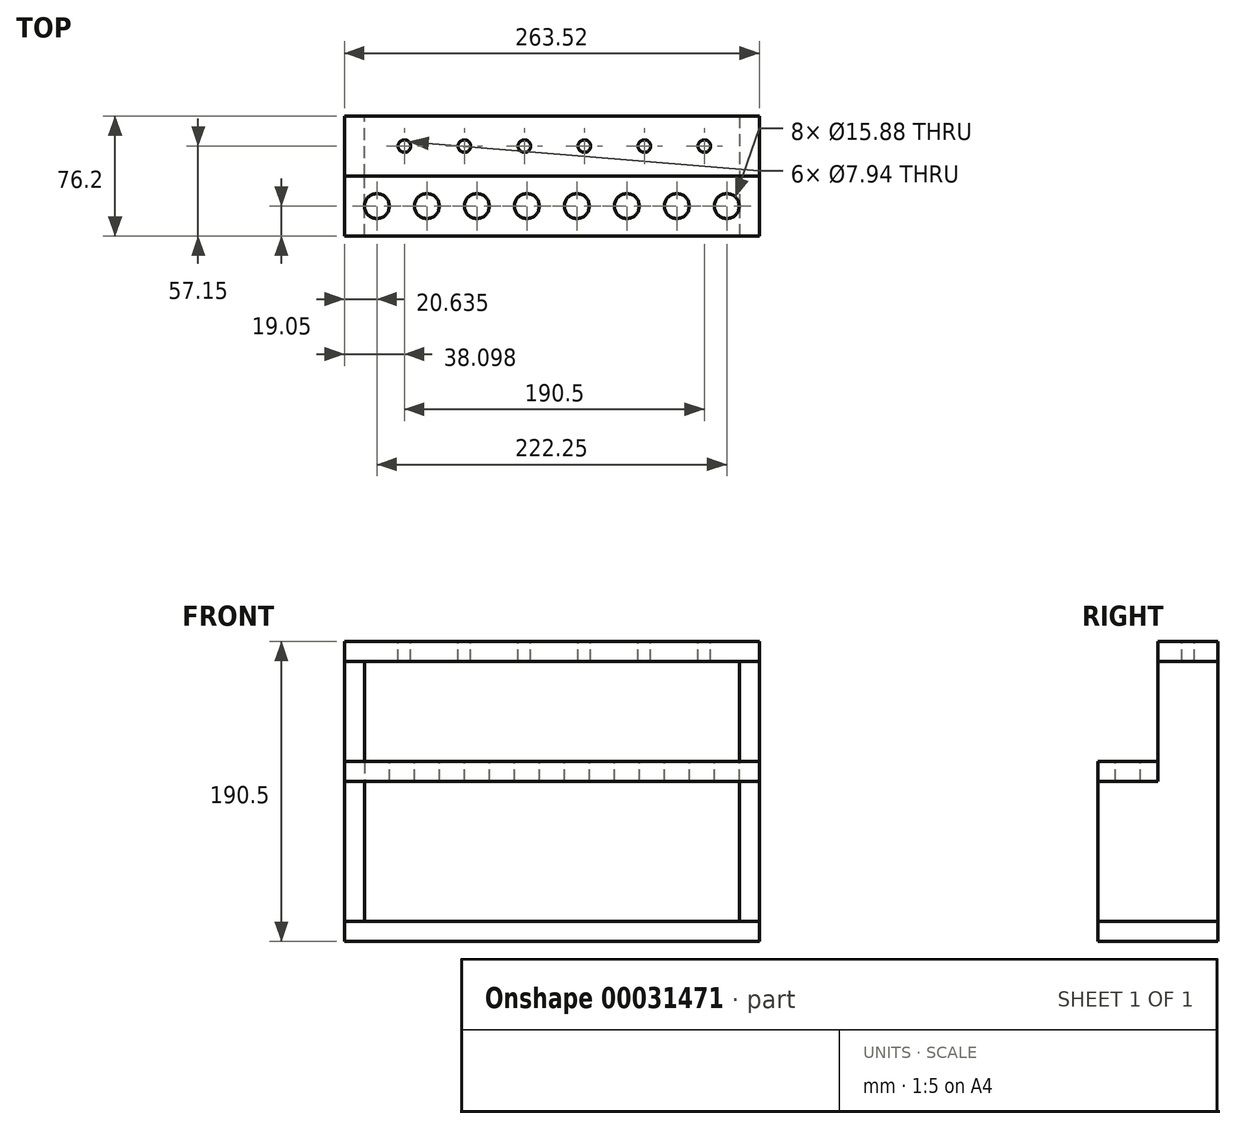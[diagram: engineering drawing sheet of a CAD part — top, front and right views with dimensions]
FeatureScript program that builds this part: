
annotation { "Feature Type Name" : "Feature", "Feature Type Description" : "" }
export const myFeature = defineFeature(function(context is Context, id is Id, definition is map)
    precondition{}
    {
        {
            var Q0;
            Q0=qCreatedBy(makeId("Top.planeOp"),FACE);
            var sketch = newSketch(context, id + "F0", { "sketchPlane" : qUnion([Q0])});
            skLineSegment(sketch, "E0.bottom", {"start": v(-189.07, 76.2) * mm, "end": v(74.45, 76.2) * mm});
            skLineSegment(sketch, "E0.top", {"start": v(-189.07, 0) * mm, "end": v(74.45, 0) * mm});
            skLineSegment(sketch, "E0.left", {"start": v(-189.07, 76.2) * mm, "end": v(-189.07, 0) * mm});
            skLineSegment(sketch, "E0.right", {"start": v(74.45, 76.2) * mm, "end": v(74.45, 0) * mm});
            skSolve(sketch);
        }
        {
            var Q0;
            Q0=makeQuery(id+"F0.imprint","IMPRINT",FACE,{"disambiguationData":[TD([[makeQuery(id+"F0.imprint","IMPRINT",EDGE,{"derivedFrom":sQuery(id+"F0.wireOp",EDGE,"E0.bottom")}),-1.0]])]});
            extrude(context, id + "F1", {"entities" : qUnion([Q0]), "depth" : 12.7 * mm});
        }
        {
            var Q0;
            Q0=makeQuery(id+"F1.opExtrude","CAP_FACE",FACE,{"disambiguationData":[OSD([sQuery(id+"F0.wireOp",EDGE,"E0.bottom"),sQuery(id+"F0.wireOp",EDGE,"E0.top"),sQuery(id+"F0.wireOp",EDGE,"E0.left"),sQuery(id+"F0.wireOp",EDGE,"E0.right")])],"isStart":false});
            var sketch = newSketch(context, id + "F2", { "sketchPlane" : qUnion([Q0])});
            skLineSegment(sketch, "E1.bottom", {"start": v(-189.07, 0) * mm, "end": v(-176.37, 0) * mm});
            skLineSegment(sketch, "E1.top", {"start": v(-189.07, 76.2) * mm, "end": v(-176.37, 76.2) * mm});
            skLineSegment(sketch, "E1.left", {"start": v(-189.07, 0) * mm, "end": v(-189.07, 76.2) * mm});
            skLineSegment(sketch, "E1.right", {"start": v(-176.37, 0) * mm, "end": v(-176.37, 76.2) * mm});
            skSolve(sketch);
        }
        {
            var Q0;
            Q0=makeQuery(id+"F2.imprint","IMPRINT",FACE,{"disambiguationData":[TD([[makeQuery(id+"F2.imprint","IMPRINT",EDGE,{"derivedFrom":sQuery(id+"F2.wireOp",EDGE,"E1.bottom")}),1.0]])]});
            extrude(context, id + "F3", {"entities" : qUnion([Q0]), "depth" : 165.1 * mm});
        }
        {
            var Q0;
            Q0=makeQuery(id+"F3.opExtrude","SWEPT_FACE",FACE,{"disambiguationData":[OSD([sQuery(id+"F2.wireOp",EDGE,"E1.right")])]});
            var sketch = newSketch(context, id + "F4", { "sketchPlane" : qUnion([Q0])});
            skLineSegment(sketch, "E2.bottom", {"start": v(0, 177.8) * mm, "end": v(38.1, 177.8) * mm});
            skLineSegment(sketch, "E2.top", {"start": v(0, 101.6) * mm, "end": v(38.1, 101.6) * mm});
            skLineSegment(sketch, "E2.left", {"start": v(0, 177.8) * mm, "end": v(0, 101.6) * mm});
            skLineSegment(sketch, "E2.right", {"start": v(38.1, 177.8) * mm, "end": v(38.1, 101.6) * mm});
            skSolve(sketch);
        }
        {
            var Q0;
            Q0=makeQuery(id+"F4.imprint","IMPRINT",FACE,{"disambiguationData":[TD([[makeQuery(id+"F4.imprint","IMPRINT",EDGE,{"derivedFrom":sQuery(id+"F4.wireOp",EDGE,"E2.bottom")}),-1.0]])]});
            extrude(context, id + "F5", {"entities" : qUnion([Q0]), "operationType" : NewBodyOperationType.REMOVE, "endBound" : BoundingType.UP_TO_NEXT, "oppositeDirection" : true, "depth" : 25.4 * mm});
        }
        {
            var Q0;
            Q0=makeQuery(id+"F1.opExtrude","CAP_FACE",FACE,{"disambiguationData":[OSD([sQuery(id+"F0.wireOp",EDGE,"E0.bottom"),sQuery(id+"F0.wireOp",EDGE,"E0.top"),sQuery(id+"F0.wireOp",EDGE,"E0.left"),sQuery(id+"F0.wireOp",EDGE,"E0.right")])],"isStart":false});
            var sketch = newSketch(context, id + "F6", { "sketchPlane" : qUnion([Q0])});
            skLineSegment(sketch, "E3.bottom", {"start": v(74.45, 76.2) * mm, "end": v(61.75, 76.2) * mm});
            skLineSegment(sketch, "E3.top", {"start": v(74.45, 0) * mm, "end": v(61.75, 0) * mm});
            skLineSegment(sketch, "E3.left", {"start": v(74.45, 76.2) * mm, "end": v(74.45, 0) * mm});
            skLineSegment(sketch, "E3.right", {"start": v(61.75, 76.2) * mm, "end": v(61.75, 0) * mm});
            skSolve(sketch);
        }
        {
            var Q0;
            Q0=makeQuery(id+"F6.imprint","IMPRINT",FACE,{"disambiguationData":[TD([[makeQuery(id+"F6.imprint","IMPRINT",EDGE,{"derivedFrom":sQuery(id+"F6.wireOp",EDGE,"E3.bottom")}),-1.0]])]});
            extrude(context, id + "F7", {"entities" : qUnion([Q0]), "depth" : 165.1 * mm});
        }
        {
            var Q0;
            Q0=makeQuery(id+"F7.opExtrude","SWEPT_FACE",FACE,{"disambiguationData":[OSD([sQuery(id+"F6.wireOp",EDGE,"E3.left")])]});
            var sketch = newSketch(context, id + "F8", { "sketchPlane" : qUnion([Q0])});
            skLineSegment(sketch, "E4.bottom", {"start": v(0, 177.8) * mm, "end": v(38.1, 177.8) * mm});
            skLineSegment(sketch, "E4.top", {"start": v(0, 101.6) * mm, "end": v(38.1, 101.6) * mm});
            skLineSegment(sketch, "E4.left", {"start": v(0, 177.8) * mm, "end": v(0, 101.6) * mm});
            skLineSegment(sketch, "E4.right", {"start": v(38.1, 177.8) * mm, "end": v(38.1, 101.6) * mm});
            skSolve(sketch);
        }
        {
            var Q0;
            Q0=makeQuery(id+"F8.imprint","IMPRINT",FACE,{"disambiguationData":[TD([[makeQuery(id+"F8.imprint","IMPRINT",EDGE,{"derivedFrom":sQuery(id+"F8.wireOp",EDGE,"E4.bottom")}),1.0]])]});
            extrude(context, id + "F9", {"entities" : qUnion([Q0]), "operationType" : NewBodyOperationType.REMOVE, "endBound" : BoundingType.UP_TO_NEXT, "oppositeDirection" : true, "depth" : 25.4 * mm});
        }
        {
            var Q0;
            Q0=makeQuery(id+"F3.opExtrude","CAP_FACE",FACE,{"disambiguationData":[OSD([sQuery(id+"F2.wireOp",EDGE,"E1.bottom"),sQuery(id+"F2.wireOp",EDGE,"E1.top"),sQuery(id+"F2.wireOp",EDGE,"E1.left"),sQuery(id+"F2.wireOp",EDGE,"E1.right")])],"isStart":false});
            var sketch = newSketch(context, id + "F10", { "sketchPlane" : qUnion([Q0])});
            skLineSegment(sketch, "E5.bottom", {"start": v(-189.07, 38.1) * mm, "end": v(74.45, 38.1) * mm});
            skLineSegment(sketch, "E5.top", {"start": v(-189.07, 76.2) * mm, "end": v(74.45, 76.2) * mm});
            skLineSegment(sketch, "E5.left", {"start": v(-189.07, 38.1) * mm, "end": v(-189.07, 76.2) * mm});
            skLineSegment(sketch, "E5.right", {"start": v(74.45, 38.1) * mm, "end": v(74.45, 76.2) * mm});
            skSolve(sketch);
        }
        {
            var Q0;
            Q0 = qSketchRegion(id + "F10", true);
            extrude(context, id + "F11", {"entities" : qUnion([Q0]), "depth" : 12.7 * mm});
        }
        {
            var Q0;
            Q0=makeQuery(id+"F5.boolean.opBoolean","COPY",FACE,{"derivedFrom":makeQuery(id+"F5.opExtrude","SWEPT_FACE",FACE,{"disambiguationData":[OSD([sQuery(id+"F4.wireOp",EDGE,"E2.top")])]})});
            var sketch = newSketch(context, id + "F12", { "sketchPlane" : qUnion([Q0])});
            skLineSegment(sketch, "E6.bottom", {"start": v(-189.07, 0) * mm, "end": v(74.45, 0) * mm});
            skLineSegment(sketch, "E6.top", {"start": v(-189.07, 38.1) * mm, "end": v(74.45, 38.1) * mm});
            skLineSegment(sketch, "E6.left", {"start": v(-189.07, 0) * mm, "end": v(-189.07, 38.1) * mm});
            skLineSegment(sketch, "E6.right", {"start": v(74.45, 0) * mm, "end": v(74.45, 38.1) * mm});
            skSolve(sketch);
        }
        {
            var Q0;
            Q0 = qSketchRegion(id + "F12", true);
            extrude(context, id + "F13", {"entities" : qUnion([Q0]), "depth" : 12.7 * mm});
        }
        {
            var Q0;
            Q0=makeQuery(id+"F13.opExtrude","CAP_FACE",FACE,{"disambiguationData":[OSD([sQuery(id+"F12.wireOp",EDGE,"E6.bottom"),sQuery(id+"F12.wireOp",EDGE,"E6.top"),sQuery(id+"F12.wireOp",EDGE,"E6.left"),sQuery(id+"F12.wireOp",EDGE,"E6.right")])],"isStart":false});
            var sketch = newSketch(context, id + "F14", { "sketchPlane" : qUnion([Q0])});
            skLineSegment(sketch, "E7", {"start": v(-189.07, 19.05) * mm, "end": v(74.45, 19.05) * mm, "construction": true});
            skCircle(sketch, "E8", {"center": v(-168.43, 19.05) * mm, "radius": 7.94 * mm});
            skCircle(sketch, "E9", {"center": v(-136.68, 19.05) * mm, "radius": 7.94 * mm});
            skCircle(sketch, "E10", {"center": v(-104.93, 19.05) * mm, "radius": 7.94 * mm});
            skCircle(sketch, "E11", {"center": v(-73.18, 19.05) * mm, "radius": 7.94 * mm});
            skCircle(sketch, "E12", {"center": v(-41.43, 19.05) * mm, "radius": 7.94 * mm});
            skCircle(sketch, "E13", {"center": v(-9.68, 19.05) * mm, "radius": 7.94 * mm});
            skCircle(sketch, "E14", {"center": v(22.07, 19.05) * mm, "radius": 7.94 * mm});
            skCircle(sketch, "E15", {"center": v(53.82, 19.05) * mm, "radius": 7.94 * mm});
            skSolve(sketch);
        }
        {
            var Q0;
            Q0 = qSketchRegion(id + "F14", true);
            extrude(context, id + "F15", {"entities" : qUnion([Q0]), "operationType" : NewBodyOperationType.REMOVE, "endBound" : BoundingType.UP_TO_NEXT, "oppositeDirection" : true, "depth" : 25.4 * mm});
        }
        {
            var Q0;
            Q0=makeQuery(id+"F11.opExtrude","CAP_FACE",FACE,{"disambiguationData":[OSD([sQuery(id+"F10.wireOp",EDGE,"E5.bottom"),sQuery(id+"F10.wireOp",EDGE,"E5.top"),sQuery(id+"F10.wireOp",EDGE,"E5.left"),sQuery(id+"F10.wireOp",EDGE,"E5.right")])],"isStart":false});
            var sketch = newSketch(context, id + "F16", { "sketchPlane" : qUnion([Q0])});
            skLineSegment(sketch, "E16", {"start": v(-189.07, 57.15) * mm, "end": v(74.45, 57.15) * mm, "construction": true});
            skCircle(sketch, "E17", {"center": v(-150.97, 57.15) * mm, "radius": 3.97 * mm});
            skCircle(sketch, "E18", {"center": v(1.43, 57.15) * mm, "radius": 3.97 * mm});
            skCircle(sketch, "E19", {"center": v(-112.87, 57.15) * mm, "radius": 3.97 * mm});
            skCircle(sketch, "E20", {"center": v(-74.77, 57.15) * mm, "radius": 3.97 * mm});
            skCircle(sketch, "E21", {"center": v(-36.67, 57.15) * mm, "radius": 3.97 * mm});
            skCircle(sketch, "E22", {"center": v(39.53, 57.15) * mm, "radius": 3.97 * mm});
            skSolve(sketch);
        }
        {
            var Q0;
            Q0 = qSketchRegion(id + "F16", true);
            extrude(context, id + "F17", {"entities" : qUnion([Q0]), "operationType" : NewBodyOperationType.REMOVE, "endBound" : BoundingType.UP_TO_NEXT, "oppositeDirection" : true, "depth" : 25.4 * mm});
        }
    });
